annotation { "Feature Type Name" : "Feature", "Feature Type Description" : "" }
export const myFeature = defineFeature(function(context is Context, id is Id, definition is map)
    precondition{}
    {
        {
            var Q0;
            Q0=qCreatedBy(makeId("Front.planeOp"),FACE);
            var sketch = newSketch(context, id + "F0", { "sketchPlane" : qUnion([Q0])});
            skLineSegment(sketch, "E0.bottom", {"start": v(-214.24, -122.3) * mm, "end": v(235.76, -122.3) * mm, "construction": true});
            skLineSegment(sketch, "E0.top", {"start": v(-214.24, 77.7) * mm, "end": v(235.76, 77.7) * mm, "construction": true});
            skLineSegment(sketch, "E0.left", {"start": v(-214.24, -122.3) * mm, "end": v(-214.24, 77.7) * mm, "construction": true});
            skLineSegment(sketch, "E0.right", {"start": v(235.76, -122.3) * mm, "end": v(235.76, -92.3) * mm, "construction": true});
            skText(sketch, "E1", { "text": "Keith Kitson\n", "fontName": "OpenSans-Regular.ttf"});
            skLineSegment(sketch, "E2", {"start": v(10.76, 19.36) * mm, "end": v(10.76, 4.36) * mm, "construction": true});
            skLineSegment(sketch, "E3", {"start": v(10.76, 4.36) * mm, "end": v(-70.91, 4.36) * mm, "construction": true});
            skLineSegment(sketch, "E4", {"start": v(-214.24, 77.7) * mm, "end": v(-258.05, 77.7) * mm, "construction": true});
            skLineSegment(sketch, "E5", {"start": v(-258.05, 77.7) * mm, "end": v(-258.05, 19.36) * mm, "construction": true});
            skLineSegment(sketch, "E6.MirrorCS", {"start": v(235.76, 77.7) * mm, "end": v(255.76, 77.7) * mm, "construction": true});
            skLineSegment(sketch, "E7.MirrorCS", {"start": v(279.57, 77.7) * mm, "end": v(279.57, 19.36) * mm, "construction": true});
            skLineSegment(sketch, "E8.MirrorCS", {"start": v(-258.05, -68.98) * mm, "end": v(-258.05, -10.64) * mm, "construction": true});
            skLineSegment(sketch, "E9.MirrorCS", {"start": v(279.57, -68.98) * mm, "end": v(279.57, -10.64) * mm, "construction": true});
            skLineSegment(sketch, "E10.MirrorCS", {"start": v(235.76, -68.98) * mm, "end": v(256.11, -68.98) * mm, "construction": true});
            skLineSegment(sketch, "E11.MirrorCS", {"start": v(-214.24, -68.98) * mm, "end": v(-258.05, -68.98) * mm, "construction": true});
            skLineSegment(sketch, "E12", {"start": v(-258.05, -10.64) * mm, "end": v(279.57, -10.64) * mm, "construction": true});
            skText(sketch, "E13", { "text": "Tunnel 2017", "fontName": "OpenSans-Regular.ttf"});
            skLineSegment(sketch, "E14", {"start": v(-214.24, 77.7) * mm, "end": v(-244.24, 77.7) * mm});
            skLineSegment(sketch, "E15", {"start": v(-244.24, 77.7) * mm, "end": v(-244.24, 82.48) * mm});
            skLineSegment(sketch, "E16", {"start": v(-219.01, 107.7) * mm, "end": v(240.53, 107.7) * mm});
            skLineSegment(sketch, "E17", {"start": v(265.76, 82.48) * mm, "end": v(265.76, -67.07) * mm});
            skLineSegment(sketch, "E18", {"start": v(240.53, -92.3) * mm, "end": v(-219.01, -92.3) * mm});
            skLineSegment(sketch, "E19", {"start": v(-244.24, -67.07) * mm, "end": v(-244.24, 77.7) * mm});
            skLineSegment(sketch, "E20.1", {"start": v(-234.24, -69.13) * mm, "end": v(-234.24, -68.98) * mm});
            skLineSegment(sketch, "E20.2", {"start": v(235.76, -82.3) * mm, "end": v(-210.46, -82.3) * mm});
            skLineSegment(sketch, "E20.3", {"start": v(255.76, 73.93) * mm, "end": v(255.76, -58.51) * mm});
            skArc(sketch, "E21", {"start": v(-244.24, 82.48) * mm, "mid": v(-226.4, 89.87) * mm, "end": v(-219.01, 107.7) * mm});
            skArc(sketch, "E22.0", {"start": v(-244.24, 72.48) * mm, "mid": v(-223.16, 79.48) * mm, "end": v(-210.46, 97.7) * mm});
            skArc(sketch, "E23.MirrorCS", {"start": v(255.76, 73.93) * mm, "mid": v(240.85, 82.8) * mm, "end": v(231.98, 97.7) * mm});
            skArc(sketch, "E24.MirrorCS", {"start": v(265.76, 82.48) * mm, "mid": v(247.92, 89.87) * mm, "end": v(240.53, 107.7) * mm});
            skLineSegment(sketch, "E25", {"start": v(-244.24, 7.7) * mm, "end": v(-194.18, 7.7) * mm, "construction": true});
            skPoint(sketch, "E25.endSnap0", {"position": v(-234.24, 7.7) * mm});
            skArc(sketch, "E26.MirrorCS", {"start": v(-244.24, -67.07) * mm, "mid": v(-226.4, -74.45) * mm, "end": v(-219.01, -92.3) * mm});
            skArc(sketch, "E27.MirrorCS", {"start": v(-244.24, -57.07) * mm, "mid": v(-223.16, -64.07) * mm, "end": v(-210.46, -82.3) * mm});
            skArc(sketch, "E28.MirrorCS", {"start": v(255.76, -58.51) * mm, "mid": v(240.85, -67.38) * mm, "end": v(231.98, -82.3) * mm});
            skArc(sketch, "E29.MirrorCS", {"start": v(265.76, -67.07) * mm, "mid": v(247.92, -74.45) * mm, "end": v(240.53, -92.3) * mm});
            skPoint(sketch, "E30.orphan", {"position": v(-209.01, -92.3) * mm});
            skPoint(sketch, "E31.orphan", {"position": v(-234.24, -82.3) * mm});
            skLineSegment(sketch, "E32.trimOffspring", {"start": v(-234.24, -58.51) * mm, "end": v(-234.24, 77.7) * mm});
            skLineSegment(sketch, "E33.trimOffspring", {"start": v(-210.46, 97.7) * mm, "end": v(231.98, 97.7) * mm});
            skPoint(sketch, "E34.orphan", {"position": v(-234.24, 97.7) * mm});
            skPoint(sketch, "E35.orphan", {"position": v(-209.01, 107.7) * mm});
            skPoint(sketch, "E36.orphan", {"position": v(230.53, 107.7) * mm});
            skLineSegment(sketch, "E37.trimOffspring", {"start": v(265.76, 77.7) * mm, "end": v(279.57, 77.7) * mm, "construction": true});
            skPoint(sketch, "E38.orphan", {"position": v(265.76, 72.48) * mm});
            skPoint(sketch, "E39.orphan", {"position": v(230.53, -92.3) * mm});
            skLineSegment(sketch, "E40.trimOffspring", {"start": v(235.76, -82.3) * mm, "end": v(235.76, 77.7) * mm, "construction": true});
            skLineSegment(sketch, "E41.trimOffspring", {"start": v(255.76, -68.98) * mm, "end": v(255.76, -69.13) * mm});
            skPoint(sketch, "E42.orphan", {"position": v(265.76, -57.07) * mm});
            skLineSegment(sketch, "E43.trimOffspring", {"start": v(265.76, -68.98) * mm, "end": v(279.57, -68.98) * mm, "construction": true});
            const initialGuessF0  = {"E1": [-0.21424, 0.01936, 1, 0, 0.05834], "E13": [-0.21424, -0.06898, 1, 0, 0.05616]};
            skSetInitialGuess(sketch, initialGuessF0);
            skSolve(sketch);
        }
        {
            var Q0;
            {var subQ17=sQuery(id+"F0.wireOp",EDGE,"E15");Q0=makeQuery(id+"F0.imprint","IMPRINT",FACE,{"disambiguationData":[TD([[makeQuery(id+"F0.imprint","IMPRINT",EDGE,{"derivedFrom":subQ17}),-1.0]])]});}
            var Q1;
            {var subQ0=sQuery(id+"F0.wireOp",EDGE,"E22.0");var subQ1=sQuery(id+"F0.wireOp",EDGE,"E19");var subQ2=makeQuery(id+"F0.imprint","INTERSECT",VERTEX,{"derivedFrom":[subQ1,subQ0]});Q1=makeQuery(id+"F0.imprint","IMPRINT",FACE,{"disambiguationData":[TD([[makeQuery(id+"F0.imprint","IMPRINT",EDGE,{"disambiguationData":[TD([[subQ2,1.0]])],"derivedFrom":subQ1}),-1.0]])]});}
            var Q2;
            {var subQ0=sQuery(id+"F0.wireOp",EDGE,"E19");var subQ5=sQuery(id+"F0.wireOp",EDGE,"E22.0");var subQ6=makeQuery(id+"F0.imprint","INTERSECT",VERTEX,{"derivedFrom":[subQ0,subQ5]});Q2=makeQuery(id+"F0.imprint","IMPRINT",FACE,{"disambiguationData":[TD([[makeQuery(id+"F0.imprint","IMPRINT",EDGE,{"disambiguationData":[TD([[subQ6,-1.0]])],"derivedFrom":subQ5}),1.0]])]});}
            var Q3;
            {var subQ0=sQuery(id+"F0.wireOp",EDGE,"E32.trimOffspring");var subQ1=sQuery(id+"F0.wireOp",EDGE,"E14");var subQ2=makeQuery(id+"F0.imprint","INTERSECT",VERTEX,{"derivedFrom":[subQ1,subQ0]});Q3=makeQuery(id+"F0.imprint","IMPRINT",FACE,{"disambiguationData":[TD([[makeQuery(id+"F0.imprint","IMPRINT",EDGE,{"disambiguationData":[TD([[subQ2,1.0]])],"derivedFrom":subQ1}),1.0]])]});}
            extrude(context, id + "F1", {"entities" : qUnion([Q0, Q1, Q2, Q3]), "depth" : 5 * mm});
        }
    });